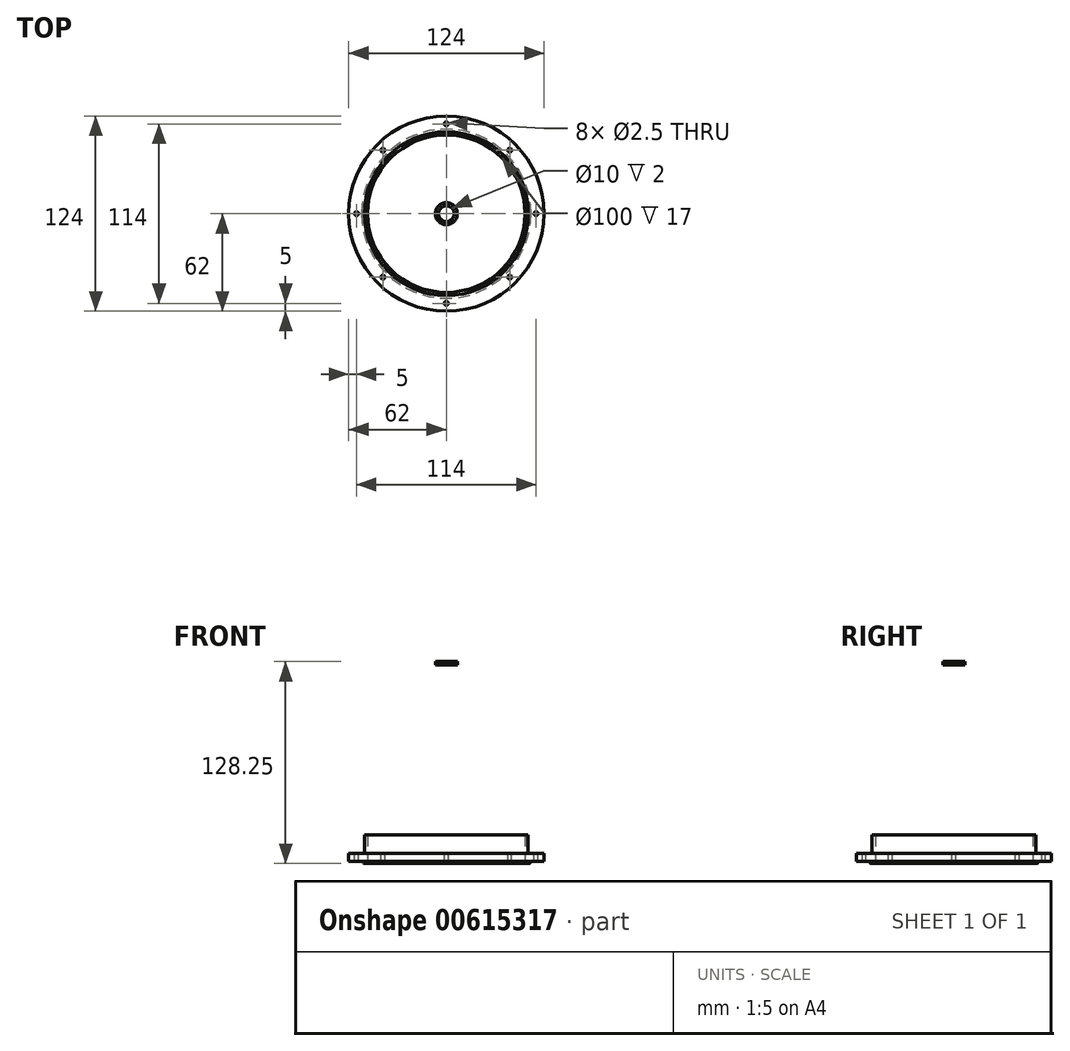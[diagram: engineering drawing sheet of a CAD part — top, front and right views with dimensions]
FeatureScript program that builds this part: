
annotation { "Feature Type Name" : "Feature", "Feature Type Description" : "" }
export const myFeature = defineFeature(function(context is Context, id is Id, definition is map)
    precondition{}
    {
        {
            var Q0;
            Q0=qCreatedBy(makeId("Top.planeOp"),FACE);
            var sketch = newSketch(context, id + "F0", { "sketchPlane" : qUnion([Q0])});
            skCircle(sketch, "E0", {"center": v(0, 0) * mm, "radius": 52 * mm});
            skSolve(sketch);
        }
        {
            var Q0;
            Q0=qSketchRegion(id+"F0",true);
            extrude(context, id + "F1", {"entities" : qUnion([Q0]), "depth" : 75 * mm, "offsetDistance" : 25 * mm});
        }
        {
            var Q0;
            Q0=makeQuery(id+"F1.opExtrude","CAP_FACE",FACE,{"disambiguationData":[OSD([sQuery(id+"F0.wireOp",EDGE,"E0")])],"isStart":false});
            var sketch = newSketch(context, id + "F2", { "sketchPlane" : qUnion([Q0])});
            skCircle(sketch, "E1", {"center": v(0, 0) * mm, "radius": 7 * mm});
            skSolve(sketch);
        }
        {
            var Q0;
            Q0=qSketchRegion(id+"F2",true);
            extrude(context, id + "F3", {"entities" : qUnion([Q0]), "depth" : 2 * mm, "offsetDistance" : 25 * mm});
        }
        {
            var Q0;
            Q0=makeQuery(id+"F3.opExtrude","SWEPT_BODY",BODY,{"disambiguationData":[OSD([sQuery(id+"F2.wireOp",EDGE,"E1")])]});
            transform(context, id + "F4", {"entities" : qUnion([Q0]), "transformType" : TransformType.TRANSLATION_3D, "dx" : 0 * mm, "dy" : 0 * mm, "dz" : 50 * mm, "makeCopy" : false});
        }
        {
            var Q0;
            Q0=makeQuery(id+"F1.opExtrude","CAP_FACE",FACE,{"disambiguationData":[OSD([sQuery(id+"F0.wireOp",EDGE,"E0")])],"isStart":false});
            var Q1;
            Q1=makeQuery(id+"F3.opExtrude","CAP_FACE",FACE,{"disambiguationData":[OSD([sQuery(id+"F2.wireOp",EDGE,"E1")])],"isStart":true});
            loft(context, id + "F5", {"sheetProfilesArray" : [{ "sheetProfileEntities" : qUnion([Q0]) }, { "sheetProfileEntities" : qUnion([Q1]) }]});
        }
        {
            var Q0;
            Q0=makeQuery(id+"F5.opLoft","SWEPT_BODY",BODY,{"disambiguationData":[OSD([sQuery(id+"F0.wireOp",EDGE,"E0"),sQuery(id+"F2.wireOp",EDGE,"E1")])]});
            var Q1;
            Q1=makeQuery(id+"F3.opExtrude","SWEPT_BODY",BODY,{"disambiguationData":[OSD([sQuery(id+"F2.wireOp",EDGE,"E1")])]});
            var Q2;
            Q2=makeQuery(id+"F1.opExtrude","SWEPT_BODY",BODY,{"disambiguationData":[OSD([sQuery(id+"F0.wireOp",EDGE,"E0")])]});
            booleanBodies(context, id + "F6", {"operationType" : BooleanOperationType.UNION, "tools" : qUnion([Q0, Q1, Q2])});
        }
        {
            var Q0;
            Q0=makeQuery(id+"F1.opExtrude","CAP_FACE",FACE,{"disambiguationData":[OSD([sQuery(id+"F0.wireOp",EDGE,"E0")])],"isStart":true});
            shell(context, id + "F7", {"entities" : qUnion([Q0]), "thickness" : 2 * mm});
        }
        {
            var Q0;
            Q0=makeQuery(id+"F3.opExtrude","CAP_FACE",FACE,{"disambiguationData":[OSD([sQuery(id+"F2.wireOp",EDGE,"E1")])],"isStart":false});
            var sketch = newSketch(context, id + "F8", { "sketchPlane" : qUnion([Q0])});
            skCircle(sketch, "E2", {"center": v(0, 0) * mm, "radius": 5 * mm});
            skSolve(sketch);
        }
        {
            var Q0;
            Q0=makeQuery(id+"F8.imprint","IMPRINT",FACE,{"disambiguationData":[TD([[makeQuery(id+"F8.imprint","IMPRINT",EDGE,{"derivedFrom":sQuery(id+"F8.wireOp",EDGE,"E2")}),1.0]])]});
            extrude(context, id + "F9", {"entities" : qUnion([Q0]), "operationType" : NewBodyOperationType.REMOVE, "oppositeDirection" : true, "depth" : 25 * mm, "offsetDistance" : 25 * mm});
        }
        {
            var Q0;
            Q0=makeQuery(id+"F1.opExtrude","CAP_FACE",FACE,{"disambiguationData":[OSD([sQuery(id+"F0.wireOp",EDGE,"E0")])],"isStart":true});
            var sketch = newSketch(context, id + "F10", { "sketchPlane" : qUnion([Q0])});
            skCircle(sketch, "E3", {"center": v(0, 0) * mm, "radius": 62 * mm});
            skSolve(sketch);
        }
        {
            var Q0;
            Q0=makeQuery(id+"F10.imprint","IMPRINT",FACE,{"disambiguationData":[TD([[makeQuery(id+"F10.imprint","IMPRINT",EDGE,{"derivedFrom":sQuery(id+"F10.wireOp",EDGE,"E3")}),1.0]])]});
            extrude(context, id + "F11", {"entities" : qUnion([Q0]), "operationType" : NewBodyOperationType.ADD, "oppositeDirection" : true, "depth" : 5 * mm, "offsetDistance" : 25 * mm});
        }
        {
            var Q0;
            Q0=makeQuery(id+"F11.opExtrude","CAP_FACE",FACE,{"disambiguationData":[OSD([sQuery(id+"F0.wireOp",EDGE,"E0"),sQuery(id+"F10.wireOp",EDGE,"E3")])],"isStart":false});
            var sketch = newSketch(context, id + "F12", { "sketchPlane" : qUnion([Q0])});
            skLineSegment(sketch, "E4", {"start": v(0, 62) * mm, "end": v(0, 52) * mm});
            skPoint(sketch, "E5", {"position": v(0, 57) * mm});
            skPoint(sketch, "E6.1.0", {"position": v(-40.3, 40.3) * mm});
            skPoint(sketch, "E6.2.0", {"position": v(-57, 0) * mm});
            skPoint(sketch, "E6.3.0", {"position": v(-40.3, -40.3) * mm});
            skPoint(sketch, "E6.4.0", {"position": v(0, -57) * mm});
            skPoint(sketch, "E6.5.0", {"position": v(40.3, -40.3) * mm});
            skPoint(sketch, "E6.6.0", {"position": v(57, 0) * mm});
            skPoint(sketch, "E6.7.0", {"position": v(40.3, 40.3) * mm});
            skPoint(sketch, "E6.center", {"position": v(0, 0) * mm});
            skSolve(sketch);
        }
        {
            var Q0;
            Q0=sQuery(id+"F12.wireOp",VERTEX,"E5");
            var Q1;
            Q1=sQuery(id+"F12.wireOp",VERTEX,"E6.7.0");
            var Q2;
            Q2=sQuery(id+"F12.wireOp",VERTEX,"E6.6.0");
            var Q3;
            Q3=sQuery(id+"F12.wireOp",VERTEX,"E6.5.0");
            var Q4;
            Q4=sQuery(id+"F12.wireOp",VERTEX,"E6.4.0");
            var Q5;
            Q5=sQuery(id+"F12.wireOp",VERTEX,"E6.3.0");
            var Q6;
            Q6=sQuery(id+"F12.wireOp",VERTEX,"E6.2.0");
            var Q7;
            Q7=sQuery(id+"F12.wireOp",VERTEX,"E6.1.0");
            var Q8;
            Q8=makeQuery(id+"F5.opLoft","SWEPT_BODY",BODY,{"disambiguationData":[OSD([sQuery(id+"F0.wireOp",EDGE,"E0"),sQuery(id+"F2.wireOp",EDGE,"E1")])]});
            hole(context, id + "F13", {"style" : HoleStyle.SIMPLE, "endStyle" : HoleEndStyle.THROUGH, "holeDiameter" : 2.5 * mm, "majorDiameter" : 5 * mm, "isTappedThrough" : true, "tappedDepth" : 12 * mm, "tapClearance" : 3, "locations" : qUnion([Q0, Q1, Q2, Q3, Q4, Q5, Q6, Q7]), "scope" : qUnion([Q8])});
        }
        {
            var Q0;
            {var subQ0=sQuery(id+"F0.wireOp",EDGE,"E0");Q0=makeQuery(id+"F11.boolean.opBoolean","MERGE",FACE,{"derivedFrom":[makeQuery(id+"F1.opExtrude","CAP_FACE",FACE,{"disambiguationData":[OSD([subQ0])],"isStart":true}),makeQuery(id+"F11.opExtrude","CAP_FACE",FACE,{"disambiguationData":[OSD([subQ0,sQuery(id+"F10.wireOp",EDGE,"E3")])],"isStart":true})]});}
            var sketch = newSketch(context, id + "F14", { "sketchPlane" : qUnion([Q0])});
            skCircle(sketch, "E7", {"center": v(0, 0) * mm, "radius": 52.5 * mm});
            skSolve(sketch);
        }
        {
            var Q0;
            Q0=qCreatedBy(makeId("Front.planeOp"),FACE);
            var sketch = newSketch(context, id + "F15", { "sketchPlane" : qUnion([Q0])});
            skCircle(sketch, "E8", {"center": v(-52.48, 0) * mm, "radius": 1.25 * mm});
            skSolve(sketch);
        }
        {
            var Q0;
            Q0=makeQuery(id+"F15.imprint","IMPRINT",FACE,{"disambiguationData":[TD([[makeQuery(id+"F15.imprint","IMPRINT",EDGE,{"derivedFrom":sQuery(id+"F15.wireOp",EDGE,"E8")}),1.0]])]});
            var Q1;
            Q1=sQuery(id+"F14.wireOp",EDGE,"E7");
            sweep(context, id + "F16", {"operationType" : NewBodyOperationType.ADD, "profiles" : qUnion([Q0]), "path" : qUnion([Q1])});
        }
        {
            var Q0;
            {var subQ0=sQuery(id+"F0.wireOp",EDGE,"E0");Q0=makeQuery(id+"F6.opBoolean","MERGE",EDGE,{"derivedFrom":[makeQuery(id+"F1.opExtrude","CAP_EDGE",EDGE,{"disambiguationData":[OSD([subQ0])],"isStart":false}),makeQuery(id+"F5.opLoft","MID_CAP_EDGE",EDGE,{"disambiguationData":[OSD([subQ0])],"capPos":0.0})]});}
            fillet(context, id + "F17", {"entities" : qUnion([Q0]), "radius" : 5 * mm, "tangentPropagation" : true, "allowEdgeOverflow" : false});
        }
        {
            var Q0;
            Q0=makeQuery(id+"F3.opExtrude","CAP_FACE",FACE,{"disambiguationData":[OSD([sQuery(id+"F2.wireOp",EDGE,"E1")])],"isStart":false});
            var sketch = newSketch(context, id + "F18", { "sketchPlane" : qUnion([Q0])});
            skLineSegment(sketch, "E9.bottom", {"start": v(77.1, -75.1) * mm, "end": v(-77.1, -75.1) * mm});
            skLineSegment(sketch, "E9.top", {"start": v(77.1, 75.1) * mm, "end": v(-77.1, 75.1) * mm});
            skLineSegment(sketch, "E9.left", {"start": v(77.1, -75.1) * mm, "end": v(77.1, 75.1) * mm});
            skLineSegment(sketch, "E9.right", {"start": v(-77.1, -75.1) * mm, "end": v(-77.1, 75.1) * mm});
            skPoint(sketch, "E9.middle", {"position": v(0, 0) * mm});
            skSolve(sketch);
        }
        {
            var Q0;
            Q0 = qSketchRegion(id + "F18", true);
            extrude(context, id + "F19", {"entities" : qUnion([Q0]), "operationType" : NewBodyOperationType.REMOVE, "oppositeDirection" : true, "depth" : 110 * mm, "offsetDistance" : 25 * mm, "hasSecondDirection" : true, "secondDirectionOppositeDirection" : true, "secondDirectionDepth" : 2 * mm});
        }
        {
            var Q0;
            Q0=makeQuery(id+"F19.boolean.opBoolean","SPLIT",BODY,{"disambiguationData":[OD(0.0)],"derivedFrom":makeQuery(id+"F5.opLoft","SWEPT_BODY",BODY,{"disambiguationData":[OSD([sQuery(id+"F0.wireOp",EDGE,"E0"),sQuery(id+"F2.wireOp",EDGE,"E1")])]})});
            transform(context, id + "F20", {"entities" : qUnion([Q0]), "transformType" : TransformType.TRANSLATION_3D, "dx" : 0 * mm, "dy" : 0 * mm, "dz" : -58 * mm, "makeCopy" : false});
        }
    });
